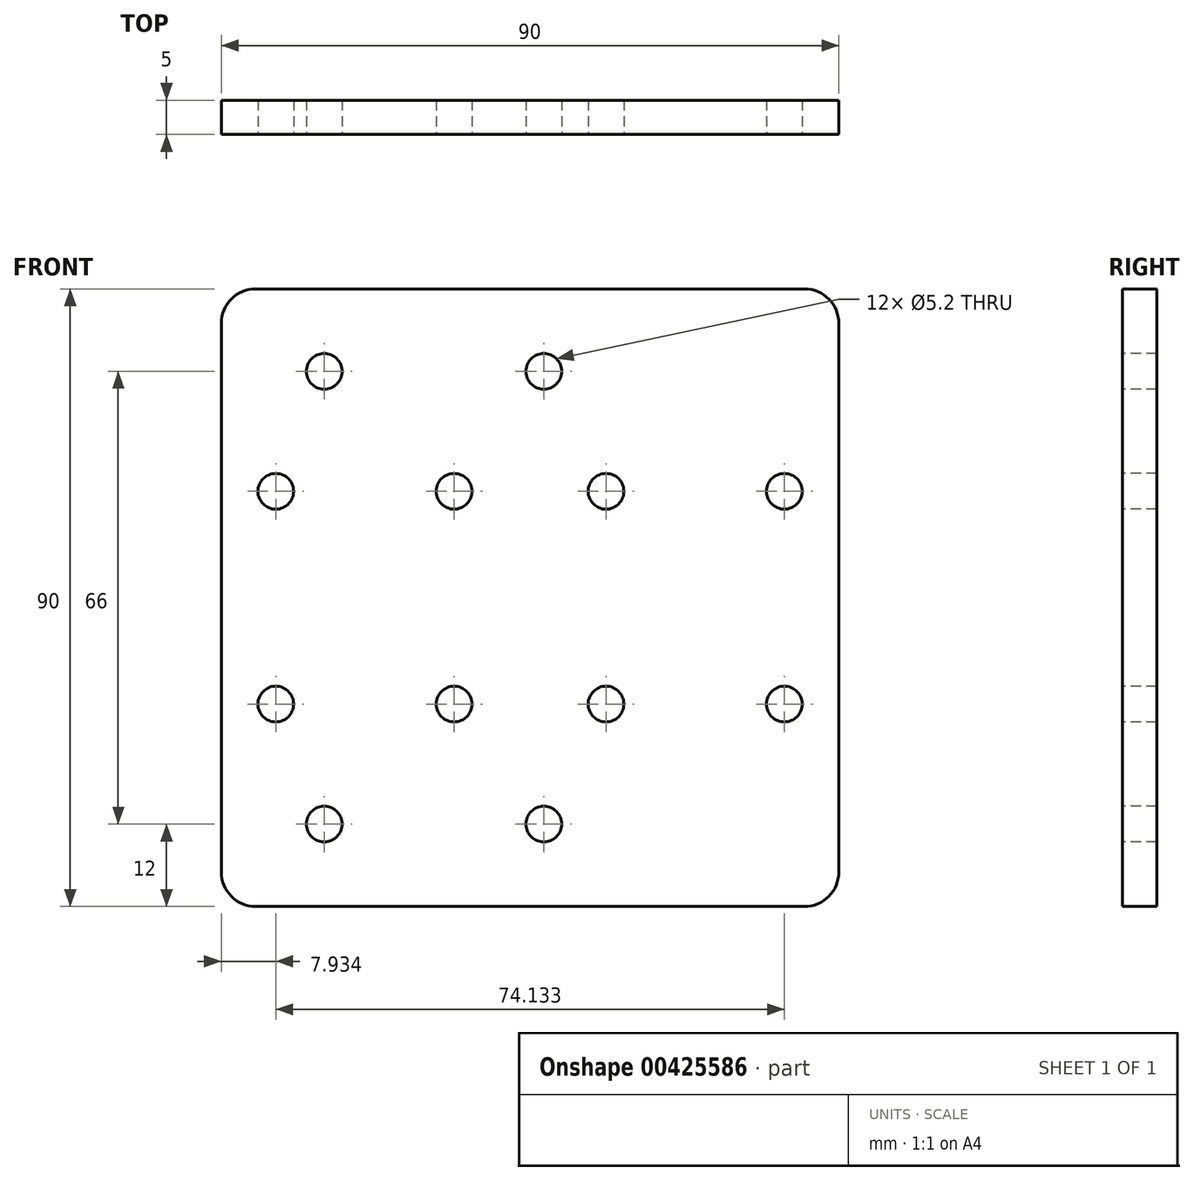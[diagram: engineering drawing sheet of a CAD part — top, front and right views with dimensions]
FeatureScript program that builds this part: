
annotation { "Feature Type Name" : "Feature", "Feature Type Description" : "" }
export const myFeature = defineFeature(function(context is Context, id is Id, definition is map)
    precondition{}
    {
        {
            var Q0;
            Q0=qCreatedBy(makeId("Front.planeOp"),FACE);
            var sketch = newSketch(context, id + "F0", { "sketchPlane" : qUnion([Q0])});
            skLineSegment(sketch, "E0.bottom", {"start": v(-45, 45) * mm, "end": v(45, 45) * mm});
            skLineSegment(sketch, "E0.top", {"start": v(-45, -45) * mm, "end": v(45, -45) * mm});
            skLineSegment(sketch, "E0.left", {"start": v(-45, 45) * mm, "end": v(-45, -45) * mm});
            skLineSegment(sketch, "E0.right", {"start": v(45, 45) * mm, "end": v(45, -45) * mm});
            skSolve(sketch);
        }
        {
            var Q0;
            Q0=makeQuery(id+"F0.imprint","IMPRINT",FACE,{"disambiguationData":[TD([[makeQuery(id+"F0.imprint","IMPRINT",EDGE,{"derivedFrom":sQuery(id+"F0.wireOp",EDGE,"E0.bottom")}),-1.0]])]});
            extrude(context, id + "F1", {"entities" : qUnion([Q0]), "depth" : 5 * mm});
        }
        {
            var Q0;
            Q0=makeQuery(id+"F1.opExtrude","CAP_FACE",FACE,{"disambiguationData":[OSD([sQuery(id+"F0.wireOp",EDGE,"E0.bottom"),sQuery(id+"F0.wireOp",EDGE,"E0.top"),sQuery(id+"F0.wireOp",EDGE,"E0.left"),sQuery(id+"F0.wireOp",EDGE,"E0.right")])],"isStart":false});
            var sketch = newSketch(context, id + "F2", { "sketchPlane" : qUnion([Q0])});
            skPoint(sketch, "E1", {"position": v(-37.07, 15.5) * mm});
            skPoint(sketch, "E2", {"position": v(-11.07, 15.5) * mm});
            skLineSegment(sketch, "E3", {"start": v(-45, 0) * mm, "end": v(45, 0) * mm});
            skLineSegment(sketch, "E4", {"start": v(0, 45) * mm, "end": v(0, -45) * mm});
            skPoint(sketch, "E5.MirrorP", {"position": v(-11.07, -15.5) * mm});
            skPoint(sketch, "E6.MirrorP", {"position": v(-37.07, -15.5) * mm});
            skPoint(sketch, "E7.MirrorP", {"position": v(11.07, 15.5) * mm});
            skPoint(sketch, "E8.MirrorP", {"position": v(37.07, 15.5) * mm});
            skPoint(sketch, "E9.MirrorP", {"position": v(37.07, -15.5) * mm});
            skPoint(sketch, "E10.MirrorP", {"position": v(11.07, -15.5) * mm});
            skSolve(sketch);
        }
        {
            var Q0;
            Q0=sQuery(id+"F2.wireOp",VERTEX,"E1");
            var Q1;
            Q1=sQuery(id+"F2.wireOp",VERTEX,"E2");
            var Q2;
            Q2=sQuery(id+"F2.wireOp",VERTEX,"E7.MirrorP");
            var Q3;
            Q3=sQuery(id+"F2.wireOp",VERTEX,"E8.MirrorP");
            var Q4;
            Q4=sQuery(id+"F2.wireOp",VERTEX,"E9.MirrorP");
            var Q5;
            Q5=sQuery(id+"F2.wireOp",VERTEX,"E10.MirrorP");
            var Q6;
            Q6=sQuery(id+"F2.wireOp",VERTEX,"E5.MirrorP");
            var Q7;
            Q7=sQuery(id+"F2.wireOp",VERTEX,"E6.MirrorP");
            var Q8;
            Q8=makeQuery(id+"F1.opExtrude","SWEPT_BODY",BODY,{"disambiguationData":[OSD([sQuery(id+"F0.wireOp",EDGE,"E0.bottom"),sQuery(id+"F0.wireOp",EDGE,"E0.top"),sQuery(id+"F0.wireOp",EDGE,"E0.left"),sQuery(id+"F0.wireOp",EDGE,"E0.right")])]});
            hole(context, id + "F3", {"style" : HoleStyle.SIMPLE, "endStyle" : HoleEndStyle.THROUGH, "holeDiameter" : 5.2 * mm, "isTappedThrough" : true, "tappedDepth" : 12 * mm, "tapClearance" : 3, "locations" : qUnion([Q0, Q1, Q2, Q3, Q4, Q5, Q6, Q7]), "scope" : qUnion([Q8])});
        }
        {
            var Q0;
            Q0=makeQuery(id+"F1.opExtrude","CAP_FACE",FACE,{"disambiguationData":[OSD([sQuery(id+"F0.wireOp",EDGE,"E0.bottom"),sQuery(id+"F0.wireOp",EDGE,"E0.top"),sQuery(id+"F0.wireOp",EDGE,"E0.left"),sQuery(id+"F0.wireOp",EDGE,"E0.right")])],"isStart":false});
            var sketch = newSketch(context, id + "F4", { "sketchPlane" : qUnion([Q0])});
            skPoint(sketch, "E11", {"position": v(-30, 33) * mm});
            skLineSegment(sketch, "E12", {"start": v(45, 0) * mm, "end": v(-45, 0) * mm});
            skPoint(sketch, "E13.MirrorP", {"position": v(-30, -33) * mm});
            skPoint(sketch, "E14", {"position": v(2, 33) * mm});
            skPoint(sketch, "E15.MirrorP", {"position": v(2, -33) * mm});
            skSolve(sketch);
        }
        {
            var Q0;
            Q0=sQuery(id+"F4.wireOp",VERTEX,"E11");
            var Q1;
            Q1=sQuery(id+"F4.wireOp",VERTEX,"E14");
            var Q2;
            Q2=sQuery(id+"F4.wireOp",VERTEX,"E15.MirrorP");
            var Q3;
            Q3=sQuery(id+"F4.wireOp",VERTEX,"E13.MirrorP");
            var Q4;
            Q4=makeQuery(id+"F1.opExtrude","SWEPT_BODY",BODY,{"disambiguationData":[OSD([sQuery(id+"F0.wireOp",EDGE,"E0.bottom"),sQuery(id+"F0.wireOp",EDGE,"E0.top"),sQuery(id+"F0.wireOp",EDGE,"E0.left"),sQuery(id+"F0.wireOp",EDGE,"E0.right")])]});
            hole(context, id + "F5", {"style" : HoleStyle.SIMPLE, "endStyle" : HoleEndStyle.THROUGH, "holeDiameter" : 5.2 * mm, "isTappedThrough" : true, "tappedDepth" : 12 * mm, "tapClearance" : 3, "locations" : qUnion([Q0, Q1, Q2, Q3]), "scope" : qUnion([Q4])});
        }
        {
            var Q0;
            Q0=makeQuery(id+"F1.opExtrude","SWEPT_EDGE",EDGE,{"disambiguationData":[OSD([sQuery(id+"F0.wireOp",EDGE,"E0.bottom"),sQuery(id+"F0.wireOp",EDGE,"E0.left")])]});
            var Q1;
            Q1=makeQuery(id+"F1.opExtrude","SWEPT_EDGE",EDGE,{"disambiguationData":[OSD([sQuery(id+"F0.wireOp",EDGE,"E0.top"),sQuery(id+"F0.wireOp",EDGE,"E0.left")])]});
            var Q2;
            Q2=makeQuery(id+"F1.opExtrude","SWEPT_EDGE",EDGE,{"disambiguationData":[OSD([sQuery(id+"F0.wireOp",EDGE,"E0.bottom"),sQuery(id+"F0.wireOp",EDGE,"E0.right")])]});
            var Q3;
            Q3=makeQuery(id+"F1.opExtrude","SWEPT_EDGE",EDGE,{"disambiguationData":[OSD([sQuery(id+"F0.wireOp",EDGE,"E0.top"),sQuery(id+"F0.wireOp",EDGE,"E0.right")])]});
            fillet(context, id + "F6", {"entities" : qUnion([Q0, Q1, Q2, Q3]), "radius" : 5 * mm, "tangentPropagation" : true, "allowEdgeOverflow" : false});
        }
    });
